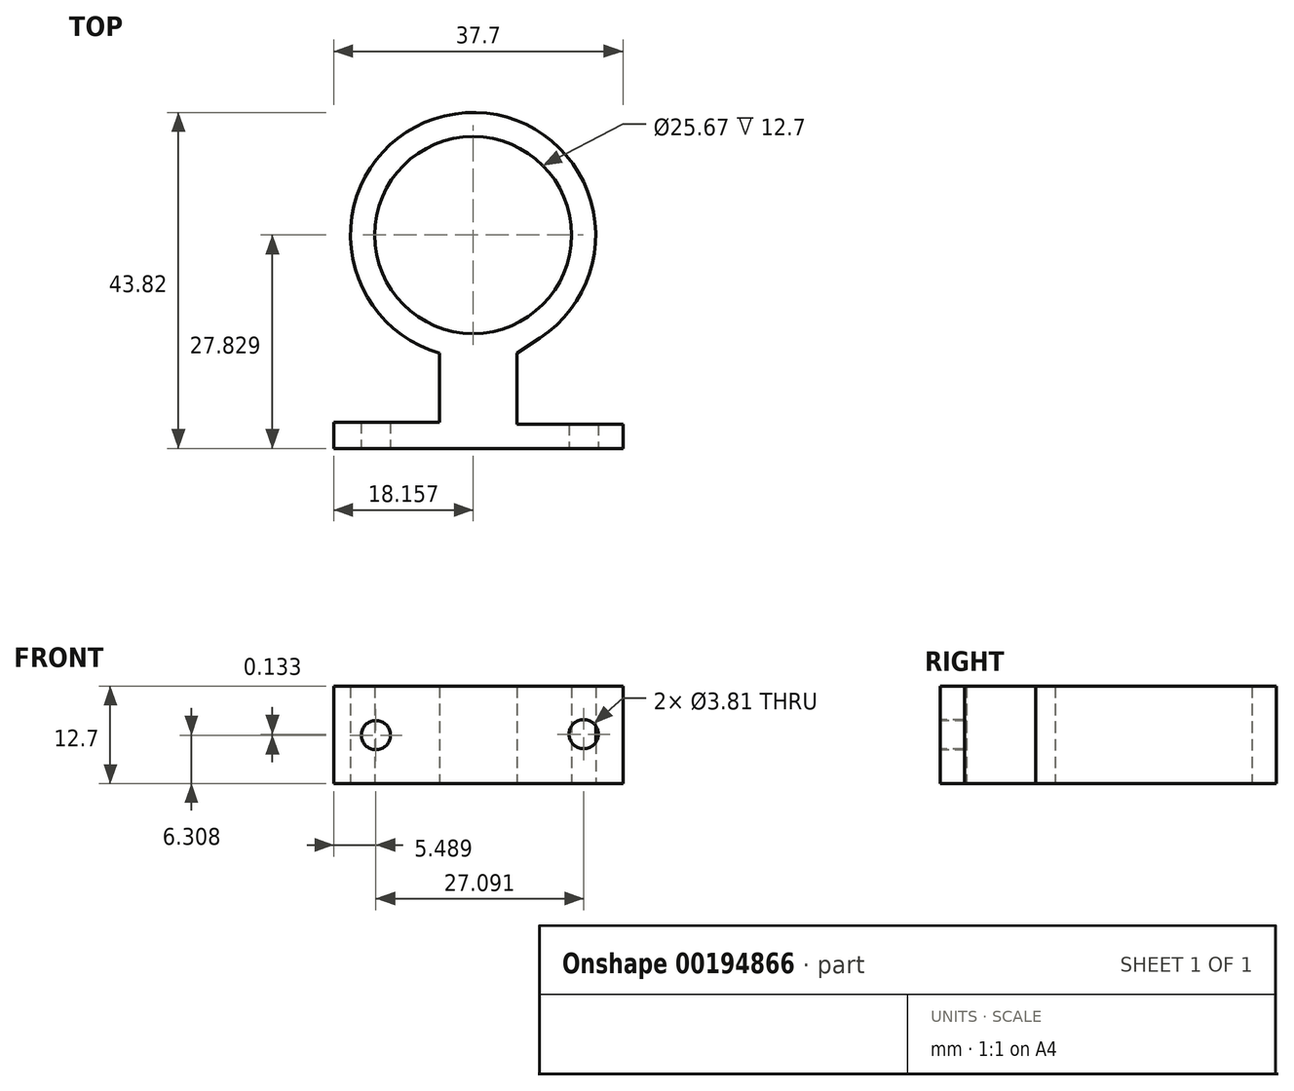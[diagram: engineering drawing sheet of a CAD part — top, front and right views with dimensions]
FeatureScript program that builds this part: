
annotation { "Feature Type Name" : "Feature", "Feature Type Description" : "" }
export const myFeature = defineFeature(function(context is Context, id is Id, definition is map)
    precondition{}
    {
        {
            var Q0;
            Q0=qCreatedBy(makeId("Top.planeOp"),FACE);
            var sketch = newSketch(context, id + "F0", { "sketchPlane" : qUnion([Q0])});
            skArc(sketch, "E0", {"start": v(-30.4, 35.48) * mm, "mid": v(-41.5, 64.69) * mm, "end": v(-43.52, 33.5) * mm});
            skLineSegment(sketch, "E1.left", {"start": v(-43.52, 33.5) * mm, "end": v(-43.52, 23.66) * mm});
            skLineSegment(sketch, "E1.right", {"start": v(-33.43, 33.5) * mm, "end": v(-33.43, 23.66) * mm});
            skLineSegment(sketch, "E2.bottom", {"start": v(-57.28, 24.22) * mm, "end": v(-43.52, 24.22) * mm});
            skLineSegment(sketch, "E2.top", {"start": v(-57.28, 21.05) * mm, "end": v(-19.58, 21.05) * mm});
            skLineSegment(sketch, "E2.left", {"start": v(-57.28, 24.22) * mm, "end": v(-57.28, 21.05) * mm});
            skLineSegment(sketch, "E2.right", {"start": v(-19.58, 24.22) * mm, "end": v(-19.58, 21.05) * mm});
            skCircle(sketch, "E3", {"center": v(-39.12, 48.88) * mm, "radius": 12.84 * mm});
            skLineSegment(sketch, "E4.trimOffspring", {"start": v(-33.43, 24.22) * mm, "end": v(-19.58, 24.22) * mm});
            skLineSegment(sketch, "E5", {"start": v(-33.43, 33.5) * mm, "end": v(-30.4, 35.48) * mm});
            skPoint(sketch, "E6.end.orphan", {"position": v(-47.84, 35.48) * mm});
            skSolve(sketch);
        }
        {
            var Q0;
            Q0 = qSketchRegion(id + "F0", true);
            extrude(context, id + "F1", {"entities" : qUnion([Q0]), "depth" : 12.7 * mm});
        }
        {
            var Q0;
            Q0=makeQuery(id+"F1.opExtrude","SWEPT_FACE",FACE,{"disambiguationData":[OSD([sQuery(id+"F0.wireOp",EDGE,"E2.top")])]});
            var sketch = newSketch(context, id + "F2", { "sketchPlane" : qUnion([Q0])});
            skCircle(sketch, "E7", {"center": v(-51.8, 6.3) * mm, "radius": 1.9 * mm});
            skCircle(sketch, "E8", {"center": v(-24.7, 6.44) * mm, "radius": 1.9 * mm});
            skSolve(sketch);
        }
        {
            var Q0;
            Q0=makeQuery(id+"F2.imprint","IMPRINT",FACE,{"disambiguationData":[TD([[makeQuery(id+"F2.imprint","IMPRINT",EDGE,{"derivedFrom":sQuery(id+"F2.wireOp",EDGE,"E7")}),1.0]])]});
            var Q1;
            Q1=makeQuery(id+"F1.opExtrude","SWEPT_FACE",FACE,{"disambiguationData":[OSD([sQuery(id+"F0.wireOp",EDGE,"E2.top")])]});
            var Q2;
            Q2=makeQuery(id+"F1.opExtrude","SWEPT_FACE",FACE,{"disambiguationData":[OSD([sQuery(id+"F0.wireOp",EDGE,"E2.bottom")])]});
            extrude(context, id + "F3", {"entities" : qUnion([Q0, Q1, Q2]), "operationType" : NewBodyOperationType.ADD, "oppositeDirection" : true, "depth" : 0.25 * mm});
        }
        {
            var Q0;
            Q0=makeQuery(id+"F2.imprint","IMPRINT",FACE,{"disambiguationData":[TD([[makeQuery(id+"F2.imprint","IMPRINT",EDGE,{"derivedFrom":sQuery(id+"F2.wireOp",EDGE,"E8")}),1.0]])]});
            var Q1;
            Q1=makeQuery(id+"F2.imprint","IMPRINT",FACE,{"disambiguationData":[TD([[makeQuery(id+"F2.imprint","IMPRINT",EDGE,{"derivedFrom":sQuery(id+"F2.wireOp",EDGE,"E7")}),1.0]])]});
            extrude(context, id + "F4", {"entities" : qUnion([Q0, Q1]), "operationType" : NewBodyOperationType.REMOVE, "oppositeDirection" : true, "depth" : 4.75 * mm});
        }
    });
